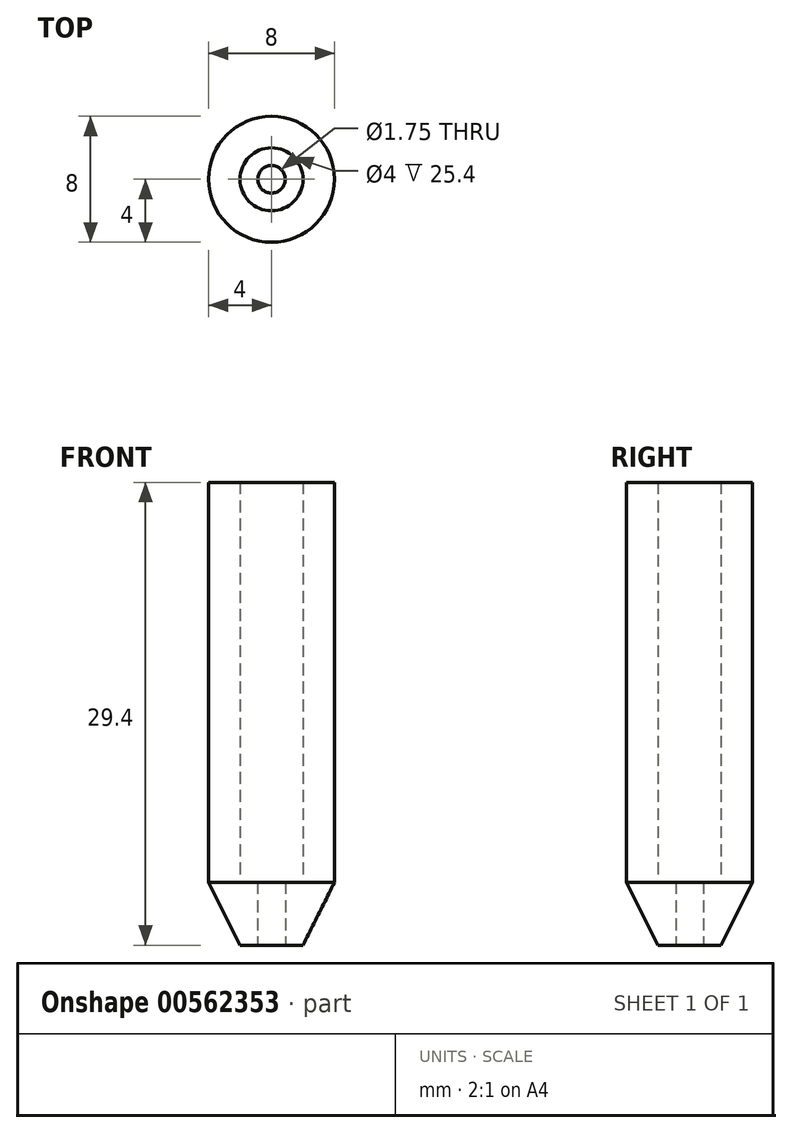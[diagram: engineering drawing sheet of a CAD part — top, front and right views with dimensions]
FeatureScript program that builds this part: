
annotation { "Feature Type Name" : "Feature", "Feature Type Description" : "" }
export const myFeature = defineFeature(function(context is Context, id is Id, definition is map)
    precondition{}
    {
        {
            var Q0;
            Q0=qCreatedBy(makeId("Top.planeOp"),FACE);
            var sketch = newSketch(context, id + "F0", { "sketchPlane" : qUnion([Q0])});
            skCircle(sketch, "E0", {"center": v(0, 0) * mm, "radius": 0.88 * mm});
            skCircle(sketch, "E1", {"center": v(0, 0) * mm, "radius": 2 * mm});
            skSolve(sketch);
        }
        {
            var Q0;
            Q0 = qSketchRegion(id + "F0", true);
            extrude(context, id + "F1", {"entities" : qUnion([Q0]), "depth" : 4 * mm, "offsetDistance" : 25.4 * mm});
        }
        {
            var Q0;
            Q0=makeQuery(id+"F1.opExtrude","CAP_FACE",FACE,{"disambiguationData":[OSD([sQuery(id+"F0.wireOp",EDGE,"E0"),sQuery(id+"F0.wireOp",EDGE,"E1")])],"isStart":false});
            var sketch = newSketch(context, id + "F2", { "sketchPlane" : qUnion([Q0])});
            skCircle(sketch, "E2", {"center": v(0, 0) * mm, "radius": 4 * mm});
            skCircle(sketch, "E3", {"center": v(0, 0) * mm, "radius": 1.3 * mm});
            skSolve(sketch);
        }
        {
            var Q0;
            Q0=makeQuery(id+"F1.opExtrude","CAP_FACE",FACE,{"disambiguationData":[OSD([sQuery(id+"F0.wireOp",EDGE,"E0"),sQuery(id+"F0.wireOp",EDGE,"E1")])],"isStart":true});
            var sketch = newSketch(context, id + "F3", { "sketchPlane" : qUnion([Q0])});
            skCircle(sketch, "E4.0", {"center": v(0, 0) * mm, "radius": 0.88 * mm});
            skCircle(sketch, "E4.1", {"center": v(0, 0) * mm, "radius": 2 * mm});
            skSolve(sketch);
        }
        {
            var Q0;
            Q0=qCreatedBy(makeId("Right.planeOp"),FACE);
            var sketch = newSketch(context, id + "F4", { "sketchPlane" : qUnion([Q0])});
            skLineSegment(sketch, "E5", {"start": v(-4, 4) * mm, "end": v(-2, 0) * mm});
            skLineSegment(sketch, "E6", {"start": v(-1.58, 0) * mm, "end": v(-1.58, 4) * mm});
            skLineSegment(sketch, "E7", {"start": v(-1.58, 4) * mm, "end": v(-4, 4) * mm});
            skLineSegment(sketch, "E8", {"start": v(-2, 0) * mm, "end": v(-1.58, 0) * mm});
            skLineSegment(sketch, "E9", {"start": v(0, 0) * mm, "end": v(0, 4) * mm});
            skSolve(sketch);
        }
        {
            var Q0;
            Q0 = qSketchRegion(id + "F4", true);
            var Q1;
            Q1=sQuery(id+"F4.wireOp",EDGE,"E9");
            revolve(context, id + "F5", {"operationType" : NewBodyOperationType.ADD, "entities" : qUnion([Q0]), "axis" : qUnion([Q1]), "revolveType" : RevolveType.FULL});
        }
        {
            var Q0;
            Q0=makeQuery(id+"F2.imprint","IMPRINT",FACE,{"disambiguationData":[TD([[makeQuery(id+"F2.imprint","IMPRINT",EDGE,{"derivedFrom":sQuery(id+"F2.wireOp",EDGE,"E2")}),1.0]])]});
            var sketch = newSketch(context, id + "F6", { "sketchPlane" : qUnion([Q0])});
            skCircle(sketch, "E10", {"center": v(0, 0) * mm, "radius": 2 * mm});
            skCircle(sketch, "E11.0", {"center": v(0, 0) * mm, "radius": 4 * mm});
            skSolve(sketch);
        }
        {
            var Q0;
            Q0 = qSketchRegion(id + "F6", true);
            extrude(context, id + "F7", {"entities" : qUnion([Q0]), "operationType" : NewBodyOperationType.ADD, "depth" : 25.4 * mm, "offsetDistance" : 25.4 * mm});
        }
    });
